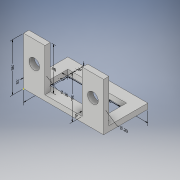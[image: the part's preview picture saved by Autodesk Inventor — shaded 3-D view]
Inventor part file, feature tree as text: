
AUTODESK INVENTOR PART (.ipt)
format: ipt  version: 2018 (Build 220112000, 112)  size: 169,472 bytes
history: native  units: in
note: dims shown in document units (in); Inventor stores cm internally (conversion verified against a paired STEP export)
features: other x16, sketch x6, extrude x3, hole x2
ambient origin geometry x8: Origin, YZ Plane, XZ Plane, XY Plane, X Axis, Y Axis, Z Axis, Center Point
bodies: Solid1 (feature_tree)
feature tree (27):
  other  "Annotations"
  sketch  "Sketch1"  dims[d0=1.5in d1=0.83in]
  extrude  "Extrusion1"  Depth=0.83in
  extrude  "Extrusion2"  Depth=0.2in
  extrude  "Extrusion3"  Depth=0.2in
  hole  "Hole1"  [1 undecoded]
  hole  "Hole2"  [1 undecoded]
  sketch  "Sketch2"  dims[d2=0.1in d3=0.0in d4=0.2in]
  sketch  "Sketch3"  dims[d5=0.2in d6=0.2in]
  sketch  "Sketch4"  dims[d7=0.2in d8=0.1in d9=0.0in]
  sketch  "Sketch5"  dims[d10=0.4in d11=0.1in]
  sketch  "Sketch6"  dims[d12=0.4in d13=0.1in d14=0.8in d15=0.0in d16=0.4in d17=0.2in d18=0.75in d19=0.375in d20=0.25in d21=0.5635in d22=1.0in d23=0.8108in d24=0.4in d25=0.2in d26=0.75in d27=0.375in d28=0.25in d29=0.5635in d30=1.0in d31=0.8108in d35=0.3131in d36=0.0777in d37=0.2in d38=0.3713in d39=0.3612in d40=0.1in d41=0.2218in d42=0.2331in d43=1.5in d44=0.0119in d45=0.1046in d46=0.83in d47=0.2802in d48=0.0806in d49=0.43in d50=0.2682in d51=0.3344in d52=1.1in d53=0.0274in d54=0.0605in d55=0.4in d56=0.0485in d57=0.0988in d58=0.4in d59=0.108in d60=0.0719in d61=0.1in d62=0.1046in d63=0.1078in d64=0.1in d65=0.3303in d66=0.1673in d67=0.8in d68=0.2768in d69=0.382in d70=0.9in d71=0.2481in d72=0.1655in d73=0.8in d74=2.2227in d75=0.2613in d76=0.0083in d77=0.2in d78=2.2531in d79=0.2099in d80=0.0459in d81=0.2in]
  other  "Linear Dimension 1"
  other  "Linear Dimension 2"
  other  "Linear Dimension 3"
  other  "Linear Dimension 4"
  other  "Linear Dimension 5"
  other  "Linear Dimension 6"
  other  "Linear Dimension 7"
  other  "Linear Dimension 8"
  other  "Linear Dimension 9"
  other  "Linear Dimension 10"
  other  "Linear Dimension 11"
  other  "Linear Dimension 12"
  other  "Linear Dimension 13"
  other  "Diameter Dimension 1"
  other  "Diameter Dimension 2"
note: 2 required parameter values undecoded (feature->parameter linkage not recoverable at this tier; creation-order binding heuristic only, values carry confidence <= 0.55)
